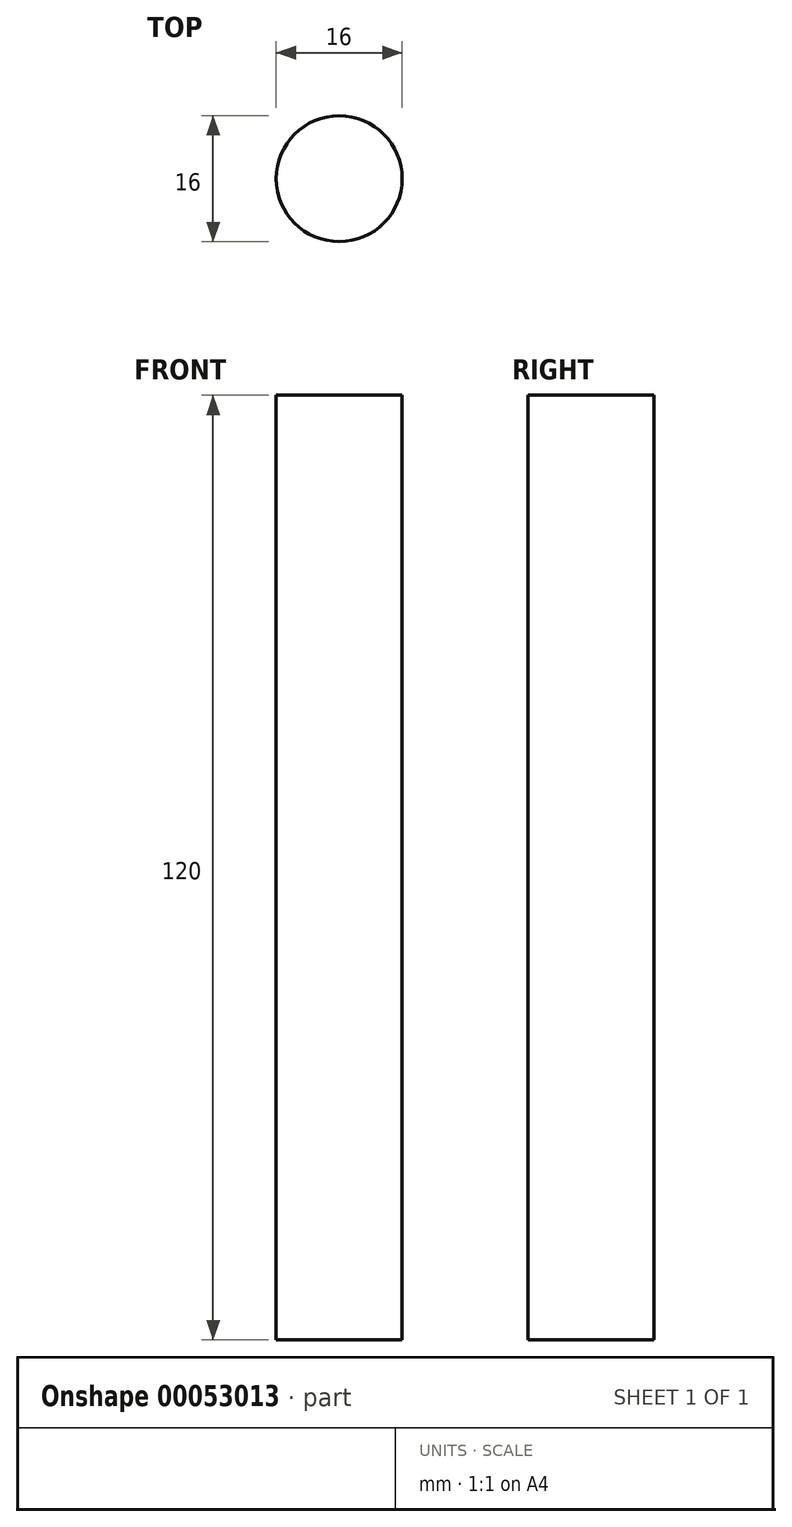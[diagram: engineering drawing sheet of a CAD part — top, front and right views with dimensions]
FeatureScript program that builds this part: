
annotation { "Feature Type Name" : "Feature", "Feature Type Description" : "" }
export const myFeature = defineFeature(function(context is Context, id is Id, definition is map)
    precondition{}
    {
        {
            var Q0;
            Q0=qCreatedBy(makeId("Top.planeOp"),FACE);
            var sketch = newSketch(context, id + "F0", { "sketchPlane" : qUnion([Q0])});
            skCircle(sketch, "E0", {"center": v(0, 0) * mm, "radius": 8 * mm});
            skSolve(sketch);
        }
        {
            var Q0;
            Q0=makeQuery(id+"F0.imprint","IMPRINT",FACE,{"disambiguationData":[TD([[makeQuery(id+"F0.imprint","IMPRINT",EDGE,{"derivedFrom":sQuery(id+"F0.wireOp",EDGE,"E0")}),1.0]])]});
            extrude(context, id + "F1", {"entities" : qUnion([Q0]), "depth" : 45 * mm, "hasSecondDirection" : true, "secondDirectionOppositeDirection" : true, "secondDirectionDepth" : 75 * mm});
        }
    });
